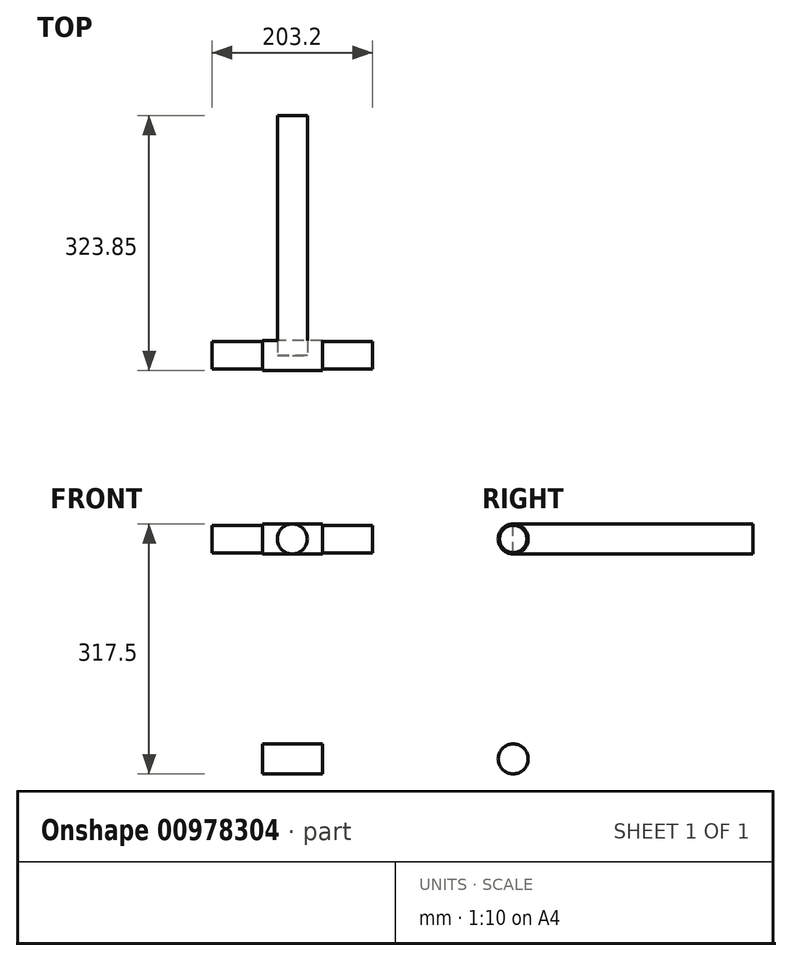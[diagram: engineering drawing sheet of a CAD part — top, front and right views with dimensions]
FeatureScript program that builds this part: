
annotation { "Feature Type Name" : "Feature", "Feature Type Description" : "" }
export const myFeature = defineFeature(function(context is Context, id is Id, definition is map)
    precondition{}
    {
        {
            var Q0;
            Q0=qCreatedBy(makeId("Right.planeOp"),FACE);
            var sketch = newSketch(context, id + "F0", { "sketchPlane" : qUnion([Q0])});
            skCircle(sketch, "E0", {"center": v(0, 139.7) * mm, "radius": 17.46 * mm});
            skCircle(sketch, "E1.MirrorC", {"center": v(0, -139.7) * mm, "radius": 17.46 * mm});
            skSolve(sketch);
        }
        {
            var Q0;
            Q0=makeQuery(id+"F0.imprint","IMPRINT",FACE,{"disambiguationData":[TD([[makeQuery(id+"F0.imprint","IMPRINT",EDGE,{"derivedFrom":sQuery(id+"F0.wireOp",EDGE,"E1.MirrorC")}),-1.0]])]});
            var Q1;
            Q1=makeQuery(id+"F0.imprint","IMPRINT",FACE,{"disambiguationData":[TD([[makeQuery(id+"F0.imprint","IMPRINT",EDGE,{"derivedFrom":sQuery(id+"F0.wireOp",EDGE,"E0")}),1.0]])]});
            extrude(context, id + "F1", {"entities" : qUnion([Q0, Q1]), "endBound" : BoundingType.SYMMETRIC, "depth" : 203.2 * mm, "offsetDistance" : 25.4 * mm});
        }
        {
            var Q0;
            Q0=qCreatedBy(makeId("Right.planeOp"),FACE);
            var sketch = newSketch(context, id + "F2", { "sketchPlane" : qUnion([Q0])});
            skCircle(sketch, "E2", {"center": v(0, 139.7) * mm, "radius": 19.05 * mm});
            skSolve(sketch);
        }
        {
            var Q0;
            Q0=makeQuery(id+"F2.imprint","IMPRINT",FACE,{"disambiguationData":[TD([[makeQuery(id+"F2.imprint","IMPRINT",EDGE,{"derivedFrom":sQuery(id+"F2.wireOp",EDGE,"E2")}),1.0]])]});
            extrude(context, id + "F3", {"entities" : qUnion([Q0]), "endBound" : BoundingType.SYMMETRIC, "depth" : 76.2 * mm, "offsetDistance" : 25.4 * mm});
        }
        {
            var Q0;
            Q0=makeQuery(id+"F3.opExtrude","SWEPT_BODY",BODY,{"disambiguationData":[OSD([sQuery(id+"F2.wireOp",EDGE,"E2")])]});
            var Q1;
            Q1=qCreatedBy(makeId("Top.planeOp"),FACE);
            mirror(context, id + "F4", {"operationType" : NewBodyOperationType.ADD, "entities" : qUnion([Q0]), "mirrorPlane" : qUnion([Q1])});
        }
        {
            var Q0;
            Q0=qCreatedBy(makeId("Front.planeOp"),FACE);
            var sketch = newSketch(context, id + "F5", { "sketchPlane" : qUnion([Q0])});
            skCircle(sketch, "E3", {"center": v(0, 139.7) * mm, "radius": 19.05 * mm});
            skSolve(sketch);
        }
        {
            var Q0;
            Q0 = qSketchRegion(id + "F5", true);
            extrude(context, id + "F6", {"entities" : qUnion([Q0]), "oppositeDirection" : true, "depth" : 304.8 * mm, "offsetDistance" : 25.4 * mm});
        }
    });
